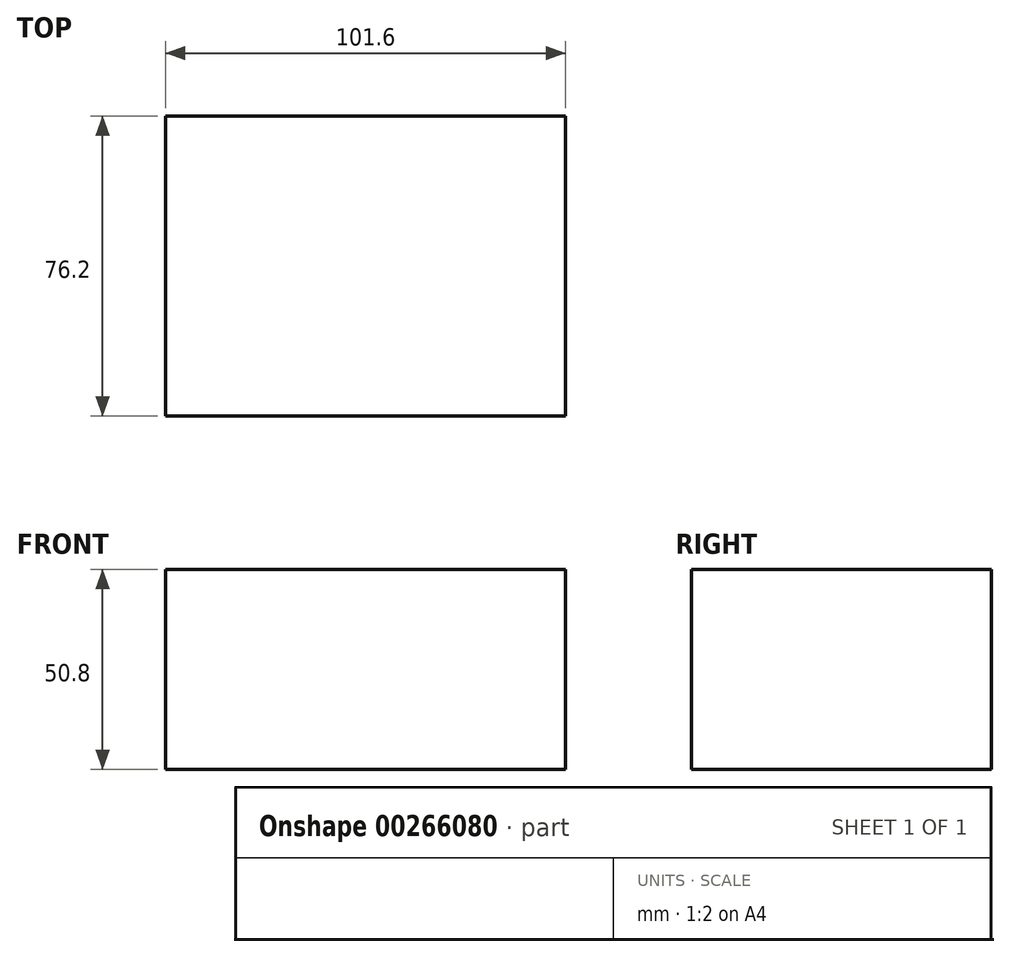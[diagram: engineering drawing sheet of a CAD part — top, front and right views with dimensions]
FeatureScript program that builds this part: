
annotation { "Feature Type Name" : "Feature", "Feature Type Description" : "" }
export const myFeature = defineFeature(function(context is Context, id is Id, definition is map)
    precondition{}
    {
        {
            var Q0;
            Q0=qCreatedBy(makeId("Front.planeOp"),FACE);
            var sketch = newSketch(context, id + "F0", { "sketchPlane" : qUnion([Q0])});
            skLineSegment(sketch, "E0.bottom", {"start": v(9.2, 68.07) * mm, "end": v(110.8, 68.07) * mm});
            skLineSegment(sketch, "E0.top", {"start": v(9.2, 17.27) * mm, "end": v(110.8, 17.27) * mm});
            skLineSegment(sketch, "E0.left", {"start": v(9.2, 68.07) * mm, "end": v(9.2, 17.27) * mm});
            skLineSegment(sketch, "E0.right", {"start": v(110.8, 68.07) * mm, "end": v(110.8, 17.27) * mm});
            skSolve(sketch);
        }
        {
            var Q0;
            Q0=makeQuery(id+"F0.imprint","IMPRINT",FACE,{"disambiguationData":[TD([[makeQuery(id+"F0.imprint","IMPRINT",EDGE,{"derivedFrom":sQuery(id+"F0.wireOp",EDGE,"E0.bottom")}),-1.0]])]});
            extrude(context, id + "F1", {"entities" : qUnion([Q0]), "depth" : 76.2 * mm});
        }
    });
